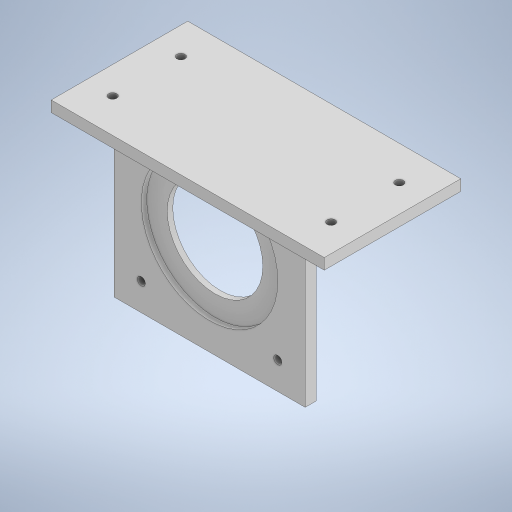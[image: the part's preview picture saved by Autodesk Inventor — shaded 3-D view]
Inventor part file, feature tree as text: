
AUTODESK INVENTOR PART (.ipt)
format: ipt  version: 2023 (Build 270158000, 158)  size: 289,792 bytes
history: native  units: mm
features: extrude x3, sketch x3, other x1
ambient origin geometry x8: Origin, YZ Plane, XZ Plane, XY Plane, X Axis, Y Axis, Z Axis, Center Point
bodies: Body1 (feature_tree)
feature tree (7):
  other  "Твердое тело1"
  extrude  "Выдавливание1"  Depth=140.0mm
  extrude  "Выдавливание2"  Depth=140.0mm
  extrude  "Выдавливание3"  Depth=100.0mm
  sketch  "Эскиз1"
  sketch  "Эскиз2"
  sketch  "Эскиз3"
